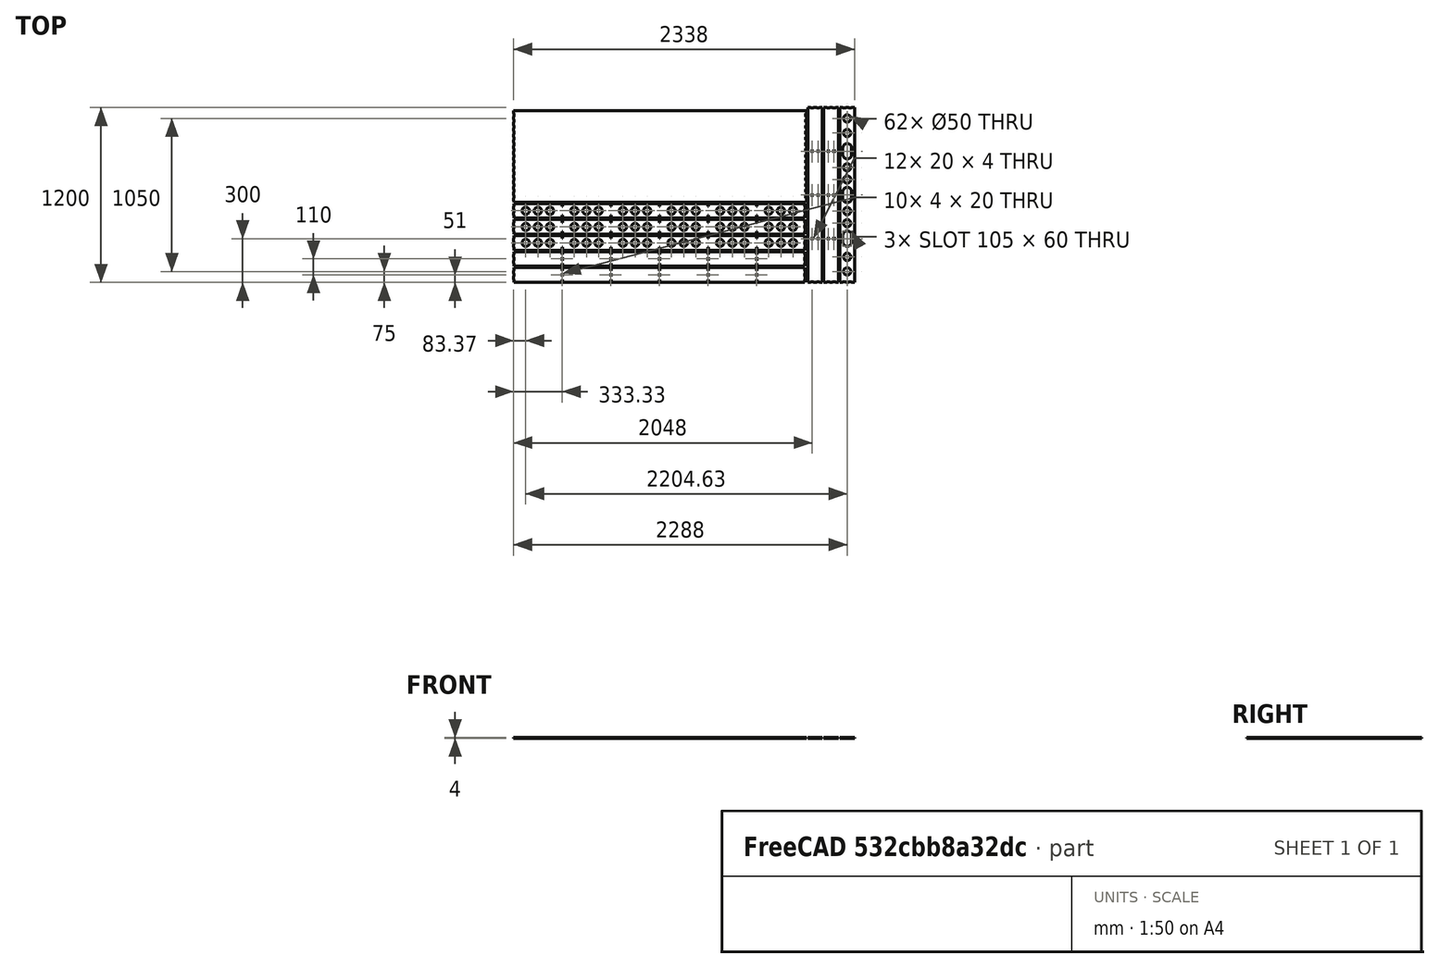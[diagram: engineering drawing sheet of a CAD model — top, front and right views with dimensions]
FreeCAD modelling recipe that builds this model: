
FCSTD DOCUMENT  (FreeCAD 0.19R24291 (Git))
Label: CAM-1
License: All rights reserved
LicenseURL: http://en.wikipedia.org/wiki/All_rights_reserved
objects: Part::Feature×9, Part::Part2DObjectPython×9
note: 18 computed .brp shape members not serialized (recipe doc carries the construction recipe); baked Part::Feature solids carry a one-line shape summary decoded from their .brp

FEATURE [Part::Feature] test  label="Framkant"
  Placement = pos=(1000,50,630) rot=(1,0,0;1.5708rad)
  shape: bbox 2000 x 100 x 4 mm, 82 faces (baked)
FEATURE [Part::Feature] test001  label="Bakkant-innre"
  Placement = pos=(1000,-60,-566) rot=(1,0,0;1.5708rad)
  shape: bbox 2000 x 100 x 4 mm, 82 faces (baked)
FEATURE [Part::Feature] test002  label="Langsprygel-3"
  Placement = pos=(1000,380,-268) rot=(1,0,0;1.5708rad)
  shape: bbox 2000 x 100 x 4 mm, 80 faces (baked)
FEATURE [Part::Feature] test003  label="Langsprygel-1"
  Placement = pos=(1000,160,32) rot=(1,0,0;1.5708rad)
  shape: bbox 2000 x 100 x 4 mm, 80 faces (baked)
FEATURE [Part::Feature] test004  label="Langsprygel-2"
  Placement = pos=(1000,270,332) rot=(1,0,0;1.5708rad)
  shape: bbox 2000 x 100 x 4 mm, 80 faces (baked)
FEATURE [Part::Feature] test005  label="Bakkant-yttre"
  Placement = pos=(1004,1015,-570) rot=(1,0,0;1.5708rad)
  shape: bbox 2008 x 627 x 4 mm, 130 faces (baked)
FEATURE [Part::Feature] test006  label="Sidkant-1"
  Placement = pos=(2068,489,-966) rot=(0,1,0;1.5708rad)
  shape: bbox 100 x 1200 x 4 mm, 46 faces (baked)
FEATURE [Part::Feature] test007  label="Sidkant-2"
  Placement = pos=(2178,489,1030) rot=(0,1,0;1.5708rad)
  shape: bbox 100 x 1200 x 4 mm, 46 faces (baked)
FEATURE [Part::Feature] test008
  Placement = pos=(2288,489,-634.66) rot=(0,1,0;1.5708rad)
  shape: bbox 100 x 1200 x 4 mm, 42 faces (baked)
FEATURE [Part::Part2DObjectPython] Shape2DView  # Draft 2D object (typed FeaturePython)
  Base = -> test
  FuseArch = false
  HiddenLines = false
  InPlace = true
  Projection = (0,0,1)
  ProjectionMode = 0
  SegmentLength = 0.05
  Tessellation = false
  VisibleOnly = false
FEATURE [Part::Part2DObjectPython] Shape2DView001  # Draft 2D object (typed FeaturePython)
  Base = -> test001
  FuseArch = false
  HiddenLines = false
  InPlace = true
  Projection = (0,0,1)
  ProjectionMode = 0
  SegmentLength = 0.05
  Tessellation = false
  VisibleOnly = false
FEATURE [Part::Part2DObjectPython] Shape2DView002  # Draft 2D object (typed FeaturePython)
  Base = -> test002
  FuseArch = false
  HiddenLines = false
  InPlace = true
  Projection = (0,0,1)
  ProjectionMode = 0
  SegmentLength = 0.05
  Tessellation = false
  VisibleOnly = false
FEATURE [Part::Part2DObjectPython] Shape2DView003  # Draft 2D object (typed FeaturePython)
  Base = -> test003
  FuseArch = false
  HiddenLines = false
  InPlace = true
  Projection = (0,0,1)
  ProjectionMode = 0
  SegmentLength = 0.05
  Tessellation = false
  VisibleOnly = false
FEATURE [Part::Part2DObjectPython] Shape2DView004  # Draft 2D object (typed FeaturePython)
  Base = -> test004
  FuseArch = false
  HiddenLines = false
  InPlace = true
  Projection = (0,0,1)
  ProjectionMode = 0
  SegmentLength = 0.05
  Tessellation = false
  VisibleOnly = false
FEATURE [Part::Part2DObjectPython] Shape2DView005  # Draft 2D object (typed FeaturePython)
  Base = -> test005
  FuseArch = false
  HiddenLines = false
  InPlace = true
  Projection = (0,0,1)
  ProjectionMode = 0
  SegmentLength = 0.05
  Tessellation = false
  VisibleOnly = false
FEATURE [Part::Part2DObjectPython] Shape2DView006  # Draft 2D object (typed FeaturePython)
  Base = -> test006
  FuseArch = false
  HiddenLines = false
  InPlace = true
  Projection = (0,0,1)
  ProjectionMode = 0
  SegmentLength = 0.05
  Tessellation = false
  VisibleOnly = false
FEATURE [Part::Part2DObjectPython] Shape2DView007  # Draft 2D object (typed FeaturePython)
  Base = -> test007
  FuseArch = false
  HiddenLines = false
  InPlace = true
  Projection = (0,0,1)
  ProjectionMode = 0
  SegmentLength = 0.05
  Tessellation = false
  VisibleOnly = false
FEATURE [Part::Part2DObjectPython] Shape2DView008  # Draft 2D object (typed FeaturePython)
  Base = -> test008
  FuseArch = false
  HiddenLines = false
  InPlace = true
  Projection = (0,0,1)
  ProjectionMode = 0
  SegmentLength = 0.05
  Tessellation = false
  VisibleOnly = false
